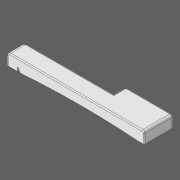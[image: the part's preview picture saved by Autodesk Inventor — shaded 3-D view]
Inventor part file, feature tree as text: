
AUTODESK INVENTOR PART (.ipt)
format: ipt  version: 2020 (Build 240168000, 168)  size: 308,736 bytes
history: native  units: in
note: dims shown in document units (in); Inventor stores cm internally (conversion verified against a paired STEP export)
features: other x4, extrude x4, fillet x2
ambient origin geometry x8: Origin, YZ Plane, XZ Plane, XY Plane, X Axis, Y Axis, Z Axis, Center Point
bodies: Solid1 (feature_tree)
feature tree (10):
  other  "FKey0"
  other  "Slot Start Plane"
  other  "Key Profile"
  extrude  "Upper (u)"  TaperAngle=0.0deg  [1 undecoded]
  extrude  "Lower (d)"  TaperAngle=0.0deg  [1 undecoded]
  extrude  "Protrusion Cutout"  Depth=0.0591in
  fillet  "Front Fillet"  Radius=0.1374in
  extrude  "Slot"  [1 undecoded]
  fillet  "Edge Softening"  Radius=0.0787in
  other  "Slot Sketch"
note: 3 required parameter values undecoded (feature->parameter linkage not recoverable at this tier; creation-order binding heuristic only, values carry confidence <= 0.55)
